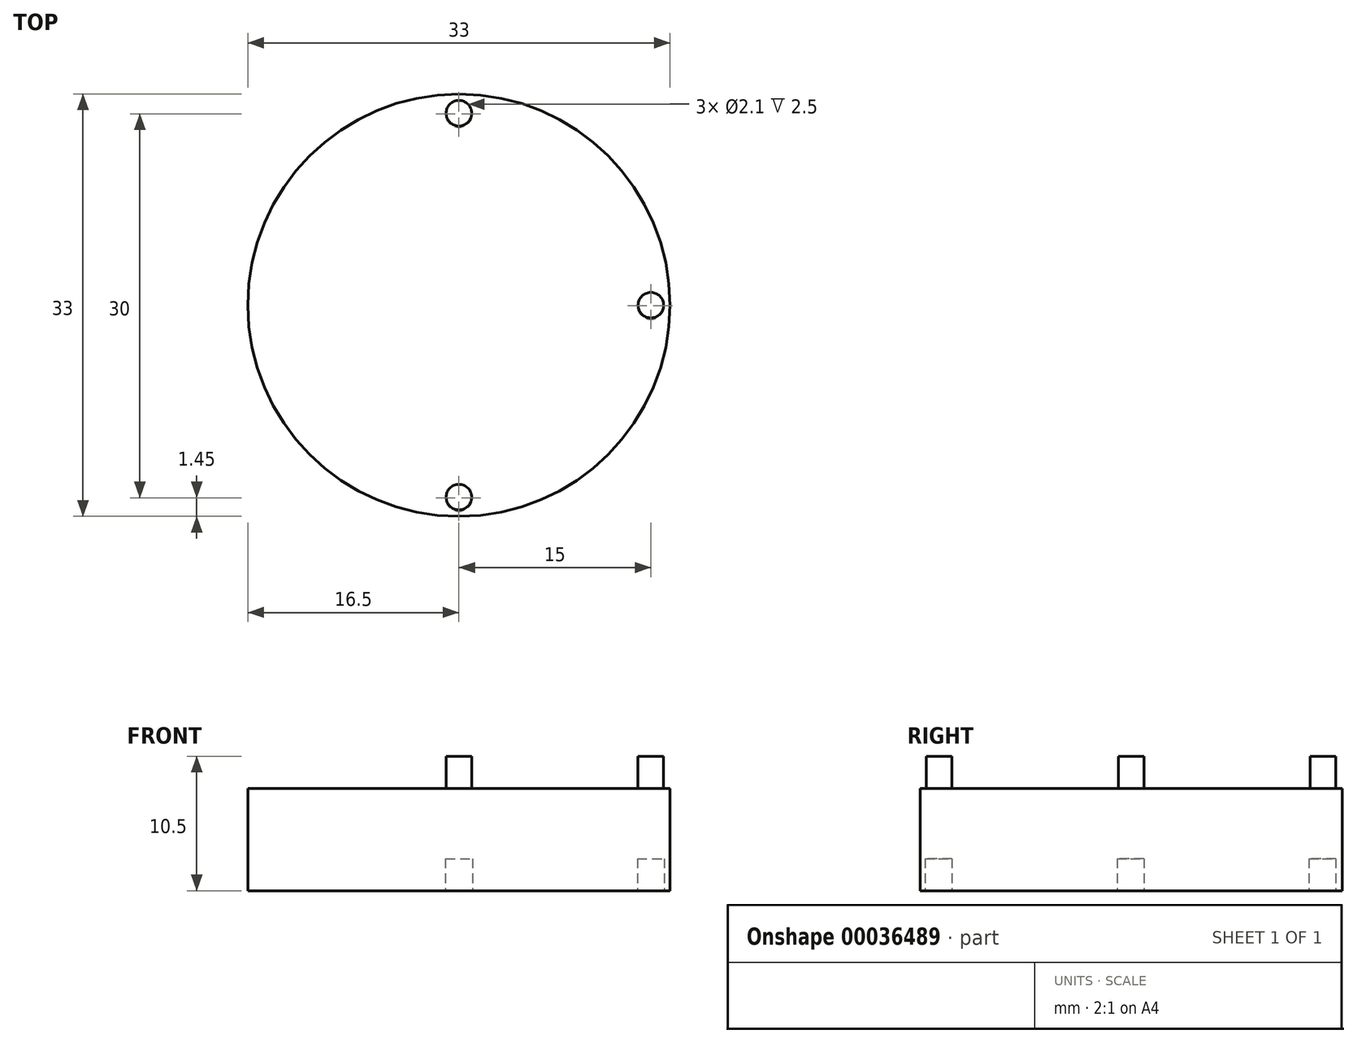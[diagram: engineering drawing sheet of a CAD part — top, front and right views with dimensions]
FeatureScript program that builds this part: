
annotation { "Feature Type Name" : "Feature", "Feature Type Description" : "" }
export const myFeature = defineFeature(function(context is Context, id is Id, definition is map)
    precondition{}
    {
        {
            var Q0;
            Q0=qCreatedBy(makeId("Top.planeOp"),FACE);
            var sketch = newSketch(context, id + "F0", { "sketchPlane" : qUnion([Q0])});
            skCircle(sketch, "E0", {"center": v(0, 0) * mm, "radius": 16.5 * mm});
            skSolve(sketch);
        }
        {
            var Q0;
            Q0=qSketchRegion(id+"F0",true);
            extrude(context, id + "F1", {"entities" : qUnion([Q0]), "depth" : 8 * mm});
        }
        {
            var Q0;
            Q0=makeQuery(id+"F1.opExtrude","CAP_FACE",FACE,{"disambiguationData":[OSD([sQuery(id+"F0.wireOp",EDGE,"E0")])],"isStart":true});
            var sketch = newSketch(context, id + "F2", { "sketchPlane" : qUnion([Q0])});
            skCircle(sketch, "E1", {"center": v(0, 15.05) * mm, "radius": 1.05 * mm});
            skCircle(sketch, "E2.1.0", {"center": v(15, 0.05) * mm, "radius": 1.05 * mm});
            skCircle(sketch, "E2.2.0", {"center": v(0, -14.95) * mm, "radius": 1.05 * mm});
            skPoint(sketch, "E2.center", {"position": v(0, 0.05) * mm});
            skLineSegment(sketch, "E2.anchor1", {"start": v(0, 0.05) * mm, "end": v(0, 15.05) * mm, "construction": true});
            skLineSegment(sketch, "E2.anchor2", {"start": v(0, 0.05) * mm, "end": v(0, -14.95) * mm, "construction": true});
            skSolve(sketch);
        }
        {
            var Q0;
            Q0=qSketchRegion(id+"F2",true);
            extrude(context, id + "F3", {"entities" : qUnion([Q0]), "operationType" : NewBodyOperationType.REMOVE, "oppositeDirection" : true, "depth" : 2.5 * mm});
        }
        {
            var Q0;
            Q0=makeQuery(id+"F1.opExtrude","CAP_FACE",FACE,{"disambiguationData":[OSD([sQuery(id+"F0.wireOp",EDGE,"E0")])],"isStart":false});
            var sketch = newSketch(context, id + "F4", { "sketchPlane" : qUnion([Q0])});
            skCircle(sketch, "E3", {"center": v(0, 15) * mm, "radius": 1 * mm});
            skCircle(sketch, "E4.1.0", {"center": v(15, 0) * mm, "radius": 1 * mm});
            skCircle(sketch, "E4.2.0", {"center": v(0, -15) * mm, "radius": 1 * mm});
            skPoint(sketch, "E4.center", {"position": v(0, 0) * mm});
            skLineSegment(sketch, "E4.anchor1", {"start": v(0, 0) * mm, "end": v(0, 15) * mm, "construction": true});
            skLineSegment(sketch, "E4.anchor2", {"start": v(0, 0) * mm, "end": v(0, -15) * mm, "construction": true});
            skSolve(sketch);
        }
        {
            var Q0;
            Q0=qSketchRegion(id+"F4",true);
            extrude(context, id + "F5", {"entities" : qUnion([Q0]), "operationType" : NewBodyOperationType.ADD, "depth" : 2.5 * mm});
        }
    });
